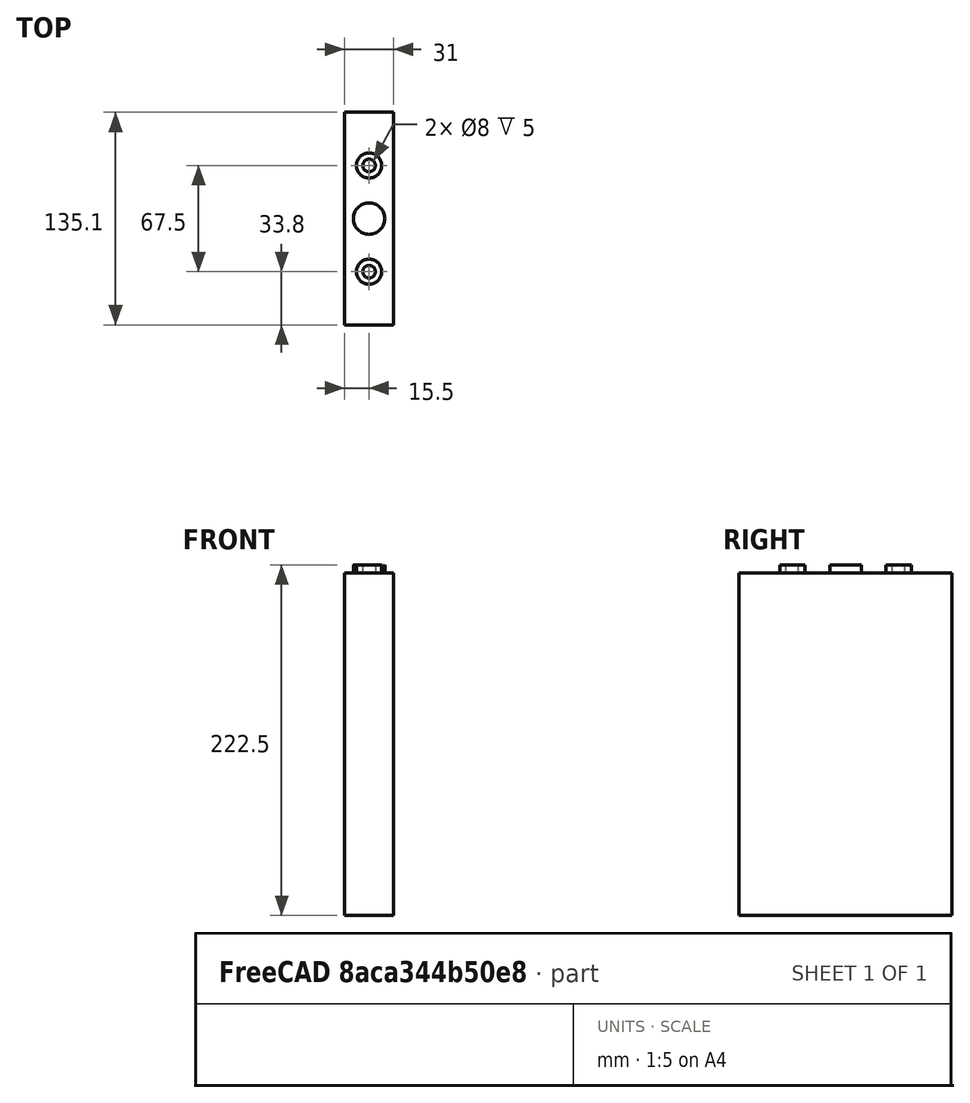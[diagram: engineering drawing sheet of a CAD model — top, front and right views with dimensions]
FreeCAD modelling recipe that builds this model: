
FCSTD DOCUMENT  (FreeCAD 0.17R9796 (Git))
Label: cam72_calb3
License: All rights reserved
LicenseURL: http://en.wikipedia.org/wiki/All_rights_reserved
objects: TechDraw::DrawViewDimension×17, TechDraw::DrawProjGroupItem×10, TechDraw::DrawProjGroup×4, Sketcher::SketchObject×3, PartDesign::Pad×2, TechDraw::DrawSVGTemplate×2, TechDraw::DrawPage×2, PartDesign::Pocket×1, PartDesign::Body×1
note: 10 computed .brp shape members not serialized (recipe doc carries the construction recipe); baked Part::Feature solids carry a one-line shape summary decoded from their .brp

FEATURE [Sketcher::SketchObject] Sketch
  MapMode = 5
  Support = -> [XY_Plane]
  sketch-geometry (4):
    g0: LineSegment StartX=0 StartY=135.1 StartZ=0 EndX=31 EndY=135.1 EndZ=0
    g1: LineSegment StartX=31 StartY=135.1 StartZ=0 EndX=31 EndY=0 EndZ=0
    g2: LineSegment StartX=31 StartY=0 StartZ=0 EndX=0 EndY=0 EndZ=0
    g3: LineSegment StartX=0 StartY=0 StartZ=0 EndX=0 EndY=135.1 EndZ=0
  constraints (11):
    c: Coincident(g0,g1)
    c: Coincident(g1,g2)
    c: Coincident(g2,g3)
    c: Coincident(g3,g0)
    c: Horizontal(g0)
    c: Horizontal(g2)
    c: Vertical(g1)
    c: Vertical(g3)
    c: Coincident(g2,g-1)
    c: DistanceY(g3,g3) = 135.1
    c: DistanceX(g2,g2) = 31
FEATURE [PartDesign::Pad] Pad
  Length = 217.3
  Length2 = 100
  Profile = -> Sketch
  Type = 0
FEATURE [Sketcher::SketchObject] Sketch001
  MapMode = 5
  Placement = pos=(0,0,217.3) rot=(0,0,1;0rad)
  Support = -> [Pad]
  sketch-geometry (3):
    g0: Circle CenterX=15.5 CenterY=33.8 CenterZ=0 NormalX=0 NormalY=0 NormalZ=1 Radius=8
    g1: Circle CenterX=15.5 CenterY=67.55 CenterZ=0 NormalX=0 NormalY=0 NormalZ=1 Radius=10
    g2: Circle CenterX=15.5 CenterY=101.3 CenterZ=0 NormalX=0 NormalY=0 NormalZ=1 Radius=8
  constraints (9):
    c: DistanceY(g-1,g1) = 67.55
    c: DistanceX(g-1,g1) = 15.5
    c: DistanceX(g-1,g0) = 15.5
    c: DistanceX(g-1,g2) = 15.5
    c: DistanceY(g-1,g0) = 33.8
    c: DistanceY(g-1,g2) = 101.3
    c: Radius(g2) = 8
    c: Radius(g0) = 8
    c: Radius(g1) = 10
FEATURE [PartDesign::Pad] Pad001
  BaseFeature = -> Pad
  Length = 5.2
  Length2 = 100
  Profile = -> Sketch001
  Type = 0
FEATURE [Sketcher::SketchObject] Sketch002
  MapMode = 5
  Placement = pos=(0,0,222.5) rot=(0,0,1;0rad)
  Support = -> [Pad001]
  sketch-geometry (2):
    g0: Circle CenterX=15.5 CenterY=101.3 CenterZ=0 NormalX=0 NormalY=0 NormalZ=1 Radius=4
    g1: Circle CenterX=15.5 CenterY=33.8 CenterZ=0 NormalX=0 NormalY=0 NormalZ=1 Radius=4
  constraints (6):
    c: Radius(g0) = 4
    c: DistanceY(g-1,g0) = 101.3
    c: DistanceX(g-1,g0) = 15.5
    c: Radius(g1) = 4
    c: DistanceX(g-1,g1) = 15.5
    c: DistanceY(g-1,g1) = 33.8
FEATURE [PartDesign::Pocket] Pocket
  BaseFeature = -> Pad001
  Length = 5
  Profile = -> Sketch002
  Type = 0
FEATURE [PartDesign::Body] Body
  Group = -> [Sketch,Pad,Sketch001,Pad001,Sketch002,Pocket]
  Origin = -> BodyOrigin
  Tip = -> Pocket
FEATURE [TechDraw::DrawSVGTemplate] Template
  Height = 210
  Orientation = 1
  Width = 297
FEATURE [TechDraw::DrawProjGroupItem] ProjItem  label="Front"
  ArcCenterMarks = true
  CenterScale = 2
  Direction = (0,-1,0)
  HardHidden = false
  HiddenWidth = 0.15
  HorizCenterLine = false
  IsoCount = 0
  IsoHidden = false
  IsoVisible = false
  IsoWidth = 0.3
  KeepLabel = false
  LineWidth = 0.7
  Rotation = 0
  RotationVector = (1,0,0)
  Scale = 0.25
  ScaleType = 2
  SeamHidden = false
  SeamVisible = false
  ShowSectionLine = true
  SmoothHidden = false
  SmoothVisible = false
  Source = -> Pocket
  Type = 0
  VertCenterLine = false
  X = -33.3707
  Y = 13.1837
FEATURE [TechDraw::DrawProjGroupItem] ProjItem001  label="Top"
  ArcCenterMarks = true
  CenterScale = 2
  Direction = (0,0,1)
  HardHidden = false
  HiddenWidth = 0.15
  HorizCenterLine = false
  IsoCount = 0
  IsoHidden = false
  IsoVisible = false
  IsoWidth = 0.3
  KeepLabel = false
  LineWidth = 0.7
  Rotation = 0
  RotationVector = (1,0,0)
  Scale = 0.25
  ScaleType = 2
  SeamHidden = false
  SeamVisible = false
  ShowSectionLine = true
  SmoothHidden = false
  SmoothVisible = false
  Source = -> Pocket
  Type = 4
  VertCenterLine = false
  X = 0
  Y = -70.625
FEATURE [TechDraw::DrawProjGroupItem] ProjItem002  label="Left"
  ArcCenterMarks = true
  CenterScale = 2
  Direction = (-1,0,0)
  HardHidden = false
  HiddenWidth = 0.15
  HorizCenterLine = false
  IsoCount = 0
  IsoHidden = false
  IsoVisible = false
  IsoWidth = 0.3
  KeepLabel = false
  LineWidth = 0.7
  Rotation = 0
  RotationVector = (0,1,0)
  Scale = 0.25
  ScaleType = 2
  SeamHidden = false
  SeamVisible = false
  ShowSectionLine = true
  SmoothHidden = false
  SmoothVisible = false
  Source = -> Pocket
  Type = 1
  VertCenterLine = false
  X = 48.775
  Y = 0
FEATURE [TechDraw::DrawProjGroup] cView
  Anchor = -> ProjItem
  AutoDistribute = true
  KeepLabel = false
  ProjectionType = 0
  Rotation = 0
  Scale = 0.25
  ScaleType = 1
  Source = -> Pocket
  Views = -> [ProjItem,ProjItem001,ProjItem002]
  X = 72.0453
  Y = 141.391
  spacingX = 15
  spacingY = 15
FEATURE [TechDraw::DrawProjGroupItem] ProjItem003  label="Front001"
  ArcCenterMarks = true
  CenterScale = 2
  Direction = (0,-1,0)
  HardHidden = false
  HiddenWidth = 0.15
  HorizCenterLine = false
  IsoCount = 0
  IsoHidden = false
  IsoVisible = false
  IsoWidth = 0.3
  KeepLabel = false
  LineWidth = 0.7
  Rotation = 0
  RotationVector = (1,0,0)
  Scale = 0.25
  ScaleType = 2
  SeamHidden = false
  SeamVisible = false
  ShowSectionLine = true
  SmoothHidden = false
  SmoothVisible = false
  Source = -> Pocket
  Type = 0
  VertCenterLine = false
  X = -61.3087
  Y = -61.3087
FEATURE [TechDraw::DrawProjGroupItem] ProjItem004  label="FrontTopRight"
  ArcCenterMarks = true
  CenterScale = 2
  Direction = (1,-1,1)
  HardHidden = false
  HiddenWidth = 0.15
  HorizCenterLine = false
  IsoCount = 0
  IsoHidden = false
  IsoVisible = false
  IsoWidth = 0.3
  KeepLabel = false
  LineWidth = 0.7
  Rotation = 0
  RotationVector = (2,-1,0.5)
  Scale = 0.25
  ScaleType = 2
  SeamHidden = false
  SeamVisible = false
  ShowSectionLine = true
  SmoothHidden = false
  SmoothVisible = false
  Source = -> Pocket
  Type = 7
  VertCenterLine = false
  X = 246.242
  Y = 246.242
FEATURE [TechDraw::DrawProjGroup] cView001
  Anchor = -> ProjItem003
  AutoDistribute = true
  KeepLabel = false
  ProjectionType = 0
  Rotation = 0
  Scale = 0.25
  ScaleType = 1
  Source = -> Pocket
  Views = -> [ProjItem003,ProjItem004]
  X = -1.65077
  Y = -119.314
  spacingX = 15
  spacingY = 15
FEATURE [TechDraw::DrawViewDimension] Dimension
  Font = Sans
  Fontsize = 4
  FormatSpec = %value%
  KeepLabel = false
  LineWidth = 0.5
  MeasureType = 1
  References2D = -> [ProjItem]
  Rotation = 0
  ScaleType = 0
  Type = 1
  X = 3.80968
  Y = -43.1763
FEATURE [TechDraw::DrawViewDimension] Dimension001
  Font = Sans
  Fontsize = 4
  FormatSpec = %value%
  KeepLabel = false
  LineWidth = 0.5
  MeasureType = 1
  References2D = -> [ProjItem]
  Rotation = 0
  ScaleType = 0
  Type = 2
  X = -20.7239
  Y = 3.08654
FEATURE [TechDraw::DrawViewDimension] Dimension002
  Font = Sans
  Fontsize = 4
  FormatSpec = %value%
  KeepLabel = false
  LineWidth = 0.5
  MeasureType = 1
  References2D = -> [ProjItem002]
  Rotation = 0
  ScaleType = 0
  Type = 1
  X = 1.69319
  Y = -43.1763
FEATURE [TechDraw::DrawViewDimension] Dimension003
  Font = Sans
  Fontsize = 4
  FormatSpec = %value%
  KeepLabel = false
  LineWidth = 0.5
  MeasureType = 1
  References2D = -> [ProjItem001]
  Rotation = 0
  ScaleType = 0
  Type = 2
  X = 26.9442
  Y = -0.960448
FEATURE [TechDraw::DrawViewDimension] Dimension004
  Font = Sans
  Fontsize = 4
  FormatSpec = %value%
  KeepLabel = false
  LineWidth = 0.5
  MeasureType = 1
  References2D = -> [ProjItem001]
  Rotation = 0
  ScaleType = 0
  Type = 2
  X = -15.1803
  Y = 0.64974
FEATURE [TechDraw::DrawViewDimension] Dimension005
  Font = Sans
  Fontsize = 4
  FormatSpec = %value%
  KeepLabel = false
  LineWidth = 0.5
  MeasureType = 1
  References2D = -> [ProjItem001]
  Rotation = 0
  ScaleType = 0
  Type = 2
  X = 6.11198
  Y = 33.9895
FEATURE [TechDraw::DrawViewDimension] Dimension006
  Font = Sans
  Fontsize = 4
  FormatSpec = ⌀%value%
  KeepLabel = false
  LineWidth = 0.5
  MeasureType = 1
  References2D = -> [ProjItem001]
  Rotation = 0
  ScaleType = 0
  Type = 5
  X = -33.805
  Y = -19.7196
FEATURE [TechDraw::DrawViewDimension] Dimension007
  Font = Sans
  Fontsize = 4
  FormatSpec = ⌀%value%
  KeepLabel = false
  LineWidth = 0.5
  MeasureType = 1
  References2D = -> [ProjItem001]
  Rotation = 0
  ScaleType = 0
  Type = 5
  X = -31.7228
  Y = 36.3771
FEATURE [TechDraw::DrawPage] Page
  ProjectionType = 0
  Template = -> Template
  Views = -> [cView,cView001,Dimension,Dimension001,Dimension002,Dimension003,Dimension004,Dimension005,Dimension006,Dimension007]
FEATURE [TechDraw::DrawSVGTemplate] Template001
  EditableTexts = Designed_by_Name=case06; Drawing_number=V.01; FC-Date=18.05.2017; FC-SC=1:3; FC-SH=1; FC-Title=COSH LibreSolarbox; Subtitle=CALB CAM72 Dimensioning; Weight=Weight
  Height = 210
  Orientation = 1
  Width = 297
FEATURE [TechDraw::DrawProjGroupItem] ProjItem005  label="Front002"
  ArcCenterMarks = true
  CenterScale = 2
  Direction = (0,-1,0)
  HardHidden = false
  HiddenWidth = 0.15
  HorizCenterLine = false
  IsoCount = 0
  IsoHidden = false
  IsoVisible = false
  IsoWidth = 0.3
  KeepLabel = false
  LineWidth = 0.7
  Rotation = 0
  RotationVector = (1,0,0)
  Scale = 0.333333
  ScaleType = 2
  SeamHidden = false
  SeamVisible = false
  ShowSectionLine = true
  SmoothHidden = false
  SmoothVisible = false
  Source = -> Pocket
  Type = 0
  VertCenterLine = false
  X = 0
  Y = 41.275
FEATURE [TechDraw::DrawProjGroupItem] ProjItem006  label="Left001"
  ArcCenterMarks = true
  CenterScale = 2
  Direction = (-1,0,0)
  HardHidden = false
  HiddenWidth = 0.15
  HorizCenterLine = false
  IsoCount = 0
  IsoHidden = false
  IsoVisible = false
  IsoWidth = 0.3
  KeepLabel = false
  LineWidth = 0.7
  Rotation = 0
  RotationVector = (0,1,0)
  Scale = 0.333333
  ScaleType = 2
  SeamHidden = false
  SeamVisible = false
  ShowSectionLine = true
  SmoothHidden = false
  SmoothVisible = false
  Source = -> Pocket
  Type = 1
  VertCenterLine = false
  X = 60.0333
  Y = 0
FEATURE [TechDraw::DrawProjGroupItem] ProjItem007  label="Top001"
  ArcCenterMarks = true
  CenterScale = 2
  Direction = (0,0,1)
  HardHidden = false
  HiddenWidth = 0.15
  HorizCenterLine = false
  IsoCount = 0
  IsoHidden = false
  IsoVisible = false
  IsoWidth = 0.3
  KeepLabel = false
  LineWidth = 0.7
  Rotation = 0
  RotationVector = (1,0,0)
  Scale = 0.333333
  ScaleType = 2
  SeamHidden = false
  SeamVisible = false
  ShowSectionLine = true
  SmoothHidden = false
  SmoothVisible = false
  Source = -> Pocket
  Type = 4
  VertCenterLine = false
  X = 0
  Y = -89.1666
FEATURE [TechDraw::DrawProjGroup] cView002
  Anchor = -> ProjItem005
  AutoDistribute = true
  KeepLabel = false
  ProjectionType = 0
  Rotation = 0
  Scale = 0.333333
  ScaleType = 2
  Source = -> Pocket
  Views = -> [ProjItem005,ProjItem006,ProjItem007]
  X = 53.349
  Y = 149.738
  spacingX = 15
  spacingY = 15
FEATURE [TechDraw::DrawViewDimension] Dimension008
  Font = Sans
  Fontsize = 4
  FormatSpec = %value%
  KeepLabel = false
  LineWidth = 0.5
  MeasureType = 1
  References2D = -> [ProjItem005]
  Rotation = 0
  ScaleType = 0
  Type = 2
  X = -37.0706
  Y = 4.46995
FEATURE [TechDraw::DrawViewDimension] Dimension009
  Font = Sans
  Fontsize = 4
  FormatSpec = %value%
  KeepLabel = false
  LineWidth = 0.5
  MeasureType = 1
  References2D = -> [ProjItem005]
  Rotation = 0
  ScaleType = 0
  Type = 2
  X = -15.2082
  Y = -21.3323
FEATURE [TechDraw::DrawViewDimension] Dimension010
  Font = Sans
  Fontsize = 4
  FormatSpec = %value%
  KeepLabel = false
  LineWidth = 0.5
  MeasureType = 1
  References2D = -> [ProjItem005]
  Rotation = 0
  ScaleType = 0
  Type = 1
  X = -20.7699
  Y = 51.2001
FEATURE [TechDraw::DrawViewDimension] Dimension011
  Font = Sans
  Fontsize = 4
  FormatSpec = %value%
  KeepLabel = false
  LineWidth = 0.5
  MeasureType = 1
  References2D = -> [ProjItem006]
  Rotation = 0
  ScaleType = 0
  Type = 1
  X = -1.44906
  Y = 50.3951
FEATURE [TechDraw::DrawViewDimension] Dimension012
  Font = Sans
  Fontsize = 4
  FormatSpec = %value%
  KeepLabel = false
  LineWidth = 0.5
  MeasureType = 1
  References2D = -> [ProjItem007]
  Rotation = 0
  ScaleType = 0
  Type = 2
  X = 41.7386
  Y = 0.674001
FEATURE [TechDraw::DrawViewDimension] Dimension013
  Font = Sans
  Fontsize = 4
  FormatSpec = %value%
  KeepLabel = false
  LineWidth = 0.5
  MeasureType = 1
  References2D = -> [ProjItem007]
  Rotation = 0
  ScaleType = 0
  Type = 2
  X = 20.1287
  Y = 6.85765
FEATURE [TechDraw::DrawViewDimension] Dimension014
  Font = Sans
  Fontsize = 4
  FormatSpec = %value%
  KeepLabel = false
  LineWidth = 0.5
  MeasureType = 1
  References2D = -> [ProjItem007]
  Rotation = 0
  ScaleType = 0
  Type = 2
  X = -17.3927
  Y = 8.85164
FEATURE [TechDraw::DrawViewDimension] Dimension015
  Font = Sans
  Fontsize = 4
  FormatSpec = ⌀%value%
  KeepLabel = false
  LineWidth = 0.5
  MeasureType = 1
  References2D = -> [ProjItem007]
  Rotation = 0
  ScaleType = 0
  Type = 5
  X = -25.6889
  Y = -19.8474
FEATURE [TechDraw::DrawViewDimension] Dimension016
  Font = Sans
  Fontsize = 4
  FormatSpec = ⌀%value%
  KeepLabel = false
  LineWidth = 0.5
  MeasureType = 1
  References2D = -> [ProjItem007]
  Rotation = 0
  ScaleType = 0
  Type = 5
  X = 31.7473
  Y = 43.7407
FEATURE [TechDraw::DrawProjGroupItem] ProjItem008  label="Front003"
  ArcCenterMarks = true
  CenterScale = 2
  Direction = (0,-1,0)
  HardHidden = false
  HiddenWidth = 0.15
  HorizCenterLine = false
  IsoCount = 0
  IsoHidden = false
  IsoVisible = false
  IsoWidth = 0.3
  KeepLabel = false
  LineWidth = 0.7
  Rotation = 0
  RotationVector = (1,0,0)
  Scale = 0.25
  ScaleType = 2
  SeamHidden = false
  SeamVisible = false
  ShowSectionLine = true
  SmoothHidden = false
  SmoothVisible = false
  Source = -> Pocket
  Type = 0
  VertCenterLine = false
  X = 0
  Y = 0
FEATURE [TechDraw::DrawProjGroupItem] ProjItem009  label="FrontTopRight001"
  ArcCenterMarks = true
  CenterScale = 2
  Direction = (1,-1,1)
  HardHidden = false
  HiddenWidth = 0.15
  HorizCenterLine = false
  IsoCount = 0
  IsoHidden = false
  IsoVisible = false
  IsoWidth = 0.3
  KeepLabel = false
  LineWidth = 0.7
  Rotation = 0
  RotationVector = (2,-1,0.5)
  Scale = 0.5
  ScaleType = 2
  SeamHidden = false
  SeamVisible = false
  ShowSectionLine = true
  SmoothHidden = false
  SmoothVisible = false
  Source = -> Pocket
  Type = 7
  VertCenterLine = false
  X = 270.097
  Y = 270.1
  expr: Scale = 0.5
FEATURE [TechDraw::DrawProjGroup] cView003
  Anchor = -> ProjItem008
  AutoDistribute = true
  KeepLabel = false
  ProjectionType = 0
  Rotation = 0
  Scale = 0.25
  ScaleType = 1
  Source = -> Pocket
  Views = -> [ProjItem008,ProjItem009]
  X = -28.6484
  Y = -137.149
  spacingX = 15
  spacingY = 15
FEATURE [TechDraw::DrawPage] Page001
  ProjectionType = 0
  Template = -> Template001
  Views = -> [cView002,Dimension008,Dimension009,Dimension010,Dimension011,Dimension012,Dimension013,Dimension014,Dimension015,Dimension016,cView003]
